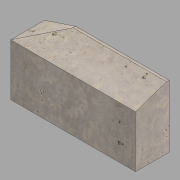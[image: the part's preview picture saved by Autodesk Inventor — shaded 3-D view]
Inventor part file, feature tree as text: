
AUTODESK INVENTOR PART (.ipt)
format: ipt  version: 2022.1 (Build 261234020, 234B)  size: 130,048 bytes
history: native  units: in
note: dims shown in document units (in); Inventor stores cm internally (conversion verified against a paired STEP export)
features: extrude x3, sketch x3
ambient origin geometry x8: Origin, YZ Plane, XZ Plane, XY Plane, X Axis, Y Axis, Z Axis, Center Point
bodies: Solid1 (feature_tree)
feature tree (6):
  extrude  "Extrusion1"  Depth=6.5in
  extrude  "Extrusion2"  Depth=12.0in
  extrude  "Extrusion3"  TaperAngle=0.0deg  [1 undecoded]
  sketch  "Sketch1"  dims[d0=24.0in d1=6.5in]
  sketch  "Sketch2"  dims[d2=12.0in d3=0.0in d4=2.0in]
  sketch  "Sketch3"  dims[d5=6.0in d6=0.0in d7=0.0in d8=6.0in d9=2.0in d10=0.0in d11=0.0in]
note: 1 required parameter value undecoded (feature->parameter linkage not recoverable at this tier; creation-order binding heuristic only, values carry confidence <= 0.55)
